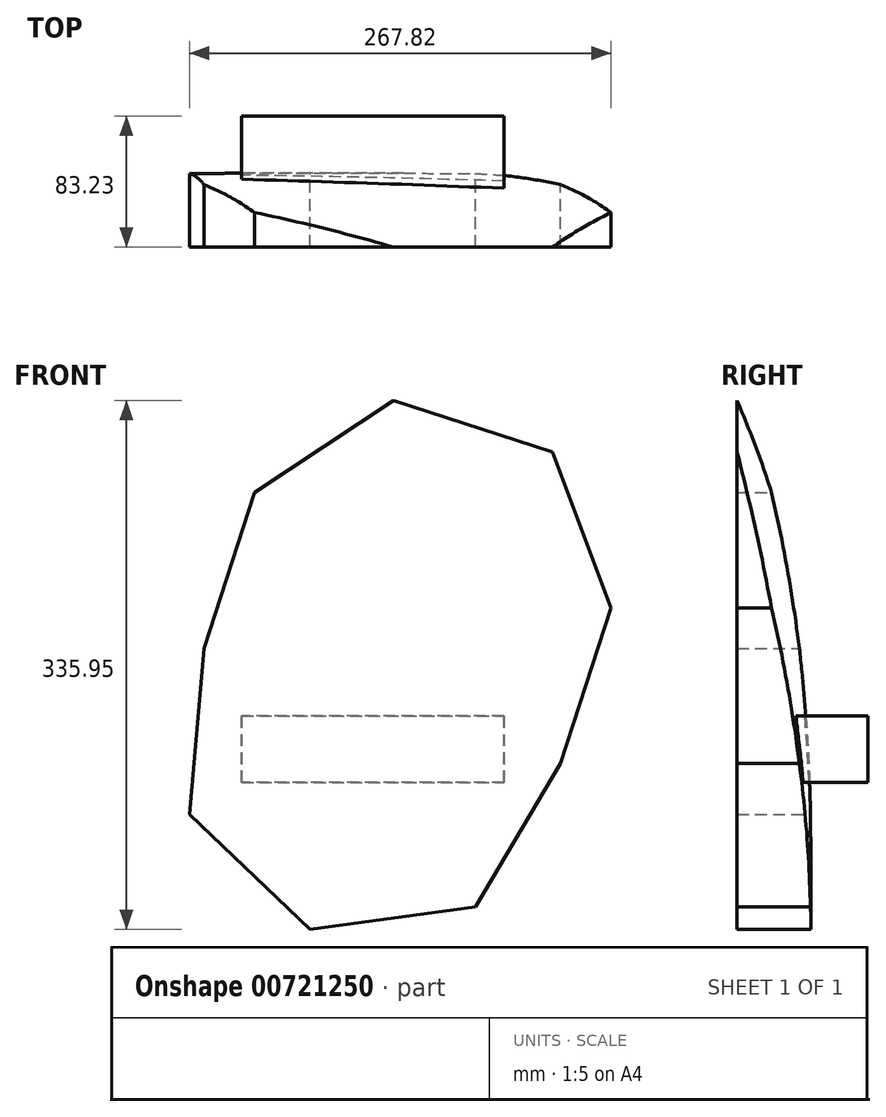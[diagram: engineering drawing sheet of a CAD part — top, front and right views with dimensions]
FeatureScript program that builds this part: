
annotation { "Feature Type Name" : "Feature", "Feature Type Description" : "" }
export const myFeature = defineFeature(function(context is Context, id is Id, definition is map)
    precondition{}
    {
        {
            var Q0;
            Q0=qCreatedBy(makeId("Front.planeOp"),FACE);
            var sketch = newSketch(context, id + "F0", { "sketchPlane" : qUnion([Q0])});
            skLineSegment(sketch, "E0.bottom", {"start": v(102.3, 41.95) * mm, "end": v(268.77, 41.95) * mm});
            skLineSegment(sketch, "E0.top", {"start": v(102.3, 0) * mm, "end": v(268.77, 0) * mm});
            skLineSegment(sketch, "E0.left", {"start": v(102.3, 41.95) * mm, "end": v(102.3, 0) * mm});
            skLineSegment(sketch, "E0.right", {"start": v(268.77, 41.95) * mm, "end": v(268.77, 0) * mm});
            skSolve(sketch);
        }
        {
            var Q0;
            Q0=makeQuery(id+"F0.imprint","IMPRINT",FACE,{"disambiguationData":[TD([[makeQuery(id+"F0.imprint","IMPRINT",EDGE,{"derivedFrom":sQuery(id+"F0.wireOp",EDGE,"E0.bottom")}),-1.0]])]});
            cPlane(context, id + "F1", {"entities" : qUnion([Q0]), "cplaneType" : CPlaneType.OFFSET, "offset" : 59.8 * mm, "width" : 152.4 * mm, "height" : 152.4 * mm});
        }
        {
            var Q0;
            Q0=makeQuery(id+"F0.imprint","IMPRINT",FACE,{"disambiguationData":[TD([[makeQuery(id+"F0.imprint","IMPRINT",EDGE,{"derivedFrom":sQuery(id+"F0.wireOp",EDGE,"E0.bottom")}),-1.0]])]});
            extrude(context, id + "F2", {"entities" : qUnion([Q0]), "depth" : 60 * mm, "offsetDistance" : 25.4 * mm});
        }
        {
            var Q0;
            Q0=qCreatedBy(id+"F1.planeOp",FACE);
            var sketch = newSketch(context, id + "F3", { "sketchPlane" : qUnion([Q0])});
            skCircle(sketch, "E1.cCircle", {"center": v(183.35, 22.61) * mm, "radius": 109.99 * mm, "construction": true});
            skLineSegment(sketch, "E1.0", {"start": v(267.6, 110.96) * mm, "end": v(304.96, 11.82) * mm});
            skLineSegment(sketch, "E1.1", {"start": v(304.96, 11.82) * mm, "end": v(250.74, -79.19) * mm});
            skLineSegment(sketch, "E1.2", {"start": v(250.74, -79.19) * mm, "end": v(145.78, -93.54) * mm});
            skLineSegment(sketch, "E1.3", {"start": v(145.78, -93.54) * mm, "end": v(69.11, -20.43) * mm});
            skLineSegment(sketch, "E1.4", {"start": v(69.11, -20.43) * mm, "end": v(78.48, 85.1) * mm});
            skLineSegment(sketch, "E1.5", {"start": v(78.48, 85.1) * mm, "end": v(166.81, 143.56) * mm});
            skLineSegment(sketch, "E1.6", {"start": v(166.81, 143.56) * mm, "end": v(267.6, 110.96) * mm});
            skPoint(sketch, "E1.0.midPoint", {"position": v(286.28, 61.39) * mm});
            skSolve(sketch);
        }
        {
            var Q0;
            Q0=makeQuery(id+"F3.imprint","IMPRINT",FACE,{"disambiguationData":[TD([[makeQuery(id+"F3.imprint","IMPRINT",EDGE,{"derivedFrom":sQuery(id+"F3.wireOp",EDGE,"E1.0")}),-1.0]])]});
            extrude(context, id + "F4", {"entities" : qUnion([Q0]), "endBound" : BoundingType.SYMMETRIC, "depth" : 46.85 * mm, "offsetDistance" : 25.4 * mm});
        }
        {
            var Q0;
            Q0=makeQuery(id+"F4.opExtrude","SWEPT_FACE",FACE,{"disambiguationData":[OSD([sQuery(id+"F3.wireOp",EDGE,"E1.6")])]});
            var Q1;
            Q1=makeQuery(id+"F4.opExtrude","SWEPT_FACE",FACE,{"disambiguationData":[OSD([sQuery(id+"F3.wireOp",EDGE,"E1.5")])]});
            var Q2;
            Q2=makeQuery(id+"F4.opExtrude","SWEPT_FACE",FACE,{"disambiguationData":[OSD([sQuery(id+"F3.wireOp",EDGE,"E1.4")])]});
            var Q3;
            Q3=makeQuery(id+"F4.opExtrude","SWEPT_FACE",FACE,{"disambiguationData":[OSD([sQuery(id+"F3.wireOp",EDGE,"E1.3")])]});
            var Q4;
            Q4=makeQuery(id+"F4.opExtrude","SWEPT_FACE",FACE,{"disambiguationData":[OSD([sQuery(id+"F3.wireOp",EDGE,"E1.2")])]});
            var Q5;
            Q5=makeQuery(id+"F4.opExtrude","SWEPT_FACE",FACE,{"disambiguationData":[OSD([sQuery(id+"F3.wireOp",EDGE,"E1.1")])]});
            var Q6;
            Q6=makeQuery(id+"F4.opExtrude","SWEPT_FACE",FACE,{"disambiguationData":[OSD([sQuery(id+"F3.wireOp",EDGE,"E1.0")])]});
            extrude(context, id + "F5", {"entities" : qUnion([Q0, Q1, Q2, Q3, Q4, Q5, Q6]), "operationType" : NewBodyOperationType.ADD, "depth" : 103.9 * mm, "offsetDistance" : 25.4 * mm});
        }
        {
            var Q0;
            {var subQ0=sQuery(id+"F3.wireOp",EDGE,"E1.6");Q0=makeQuery(id+"F5.opExtrude","CAP_EDGE",EDGE,{"disambiguationData":[OSD([subQ0]),TDD([makeQuery(id+"F4.opExtrude","CAP_EDGE",EDGE,{"disambiguationData":[OSD([subQ0])],"isStart":true})])],"isStart":false});}
            fillet(context, id + "F6", {"entities" : qUnion([Q0]), "radius" : 1048.4 * mm, "tangentPropagation" : true, "allowEdgeOverflow" : false});
        }
    });
